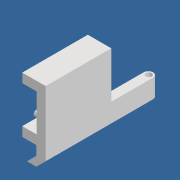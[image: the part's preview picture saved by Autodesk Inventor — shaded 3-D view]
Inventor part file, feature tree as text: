
AUTODESK INVENTOR PART (.ipt)
format: ipt  version: 2020 (Build 240168000, 168)  size: 212,992 bytes
history: native  units: mm
features: sketch x10, extrude x9, chamfer x2, split x1, fillet x1
ambient origin geometry x8: Origin, YZ Plane, XZ Plane, XY Plane, X Axis, Y Axis, Z Axis, Center Point
bodies: Solid1 (feature_tree)
feature tree (23):
  extrude  "Extrusion1"  Depth=56.0mm
  extrude  "Extrusion2"  Depth=40.0mm
  extrude  "Extrusion3"  Depth=7.8mm
  extrude  "Extrusion4"  Depth=4.6mm
  sketch  "Sketch14"  dims[d10=4.6mm d11=16.0mm]
  extrude  "Extrusion7"  Depth=16.0mm
  extrude  "Extrusion8"  Depth=12.0mm TaperAngle=0.0deg
  chamfer  "Chamfer1"  Distance=26.0mm
  chamfer  "Chamfer2"  Distance=24.0mm
  split  "Split2"
  extrude  "Extrusion9"  Depth=8.0mm
  extrude  "Extrusion13"  Depth=8.0mm
  extrude  "Extrusion14"  Depth=8.0mm
  fillet  "Fillet2"  Radius=8.0mm
  sketch  "Sketch1"  dims[d0=39.6mm d1=56.0mm]
  sketch  "Sketch2"  dims[d2=40.0mm d3=0.0mm d4=24.4mm]
  sketch  "Sketch3"  dims[d5=31.8mm d6=7.8mm]
  sketch  "Sketch4"  dims[d7=64.0mm d8=0.0mm d9=4.6mm]
  sketch  "Sketch15"  dims[d12=12.0mm d13=26.0mm d14=0.0mm]
  sketch  "Sketch16"  dims[d15=24.0mm]
  sketch  "Sketch17"  dims[d16=8.0mm d17=26.0mm d18=0.0mm d35=24.0mm d36=0.0mm]
  sketch  "Sketch22"  dims[d37=24.0mm d38=8.0mm]
  sketch  "Sketch23"  dims[d39=8.0mm d40=8.0mm d41=8.0mm d42=8.0mm d43=16.0mm d44=0.0mm d45=0.0mm d46=8.0mm d47=2.0mm d48=45.0deg d49=8.0mm d50=2.0mm d51=45.0deg d52=5.0mm d53=5.0mm d55=5.0mm d56=5.0mm d57=5.0mm d58=5.0mm d59=16.0mm d60=16.0mm d61=40.0mm d62=4.0mm d63=12.0mm d64=8.0mm d65=0.0mm d82=8.0mm d83=16.0mm d84=39.7mm d85=0.0mm d86=5.0mm d87=4.0mm d88=3.7mm d89=0.0mm d90=0.0mm d91=4.0mm d92=14.3117mm d93=0.75mm d94=20.594885mm d95=0.0625mm d96=0.75mm d97=0.375mm]
